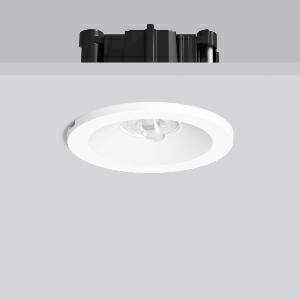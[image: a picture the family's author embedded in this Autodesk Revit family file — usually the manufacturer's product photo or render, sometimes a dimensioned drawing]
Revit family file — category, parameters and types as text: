
# Revit family: turia_l_672561_002_07_3232
name_source: partatom
category: Lighting Fixtures
units: mm (PartAtom-declared; Revit-internal decimal feet)

## family parameters
Cut with Voids When Loaded = No
Host = Face
Light Source = No
Part Type = Normal
Room Calculation Point = No
Round Connector Dimension = Use Diameter
Shared = No

## types (1)
- TURIA L (1 x LED Modul 765, 270 lm, 6500)
    Apparent Load = 5 VA
    CIE Flux Codes = 70 91 99 100 100
    Color Rendering = 70
    Color Temperature = 6500
    Default Elevation = 1800 mm
    Description = Series: TURIA L
Round emergency luminaire for escape route lighting. Housing: die-cast aluminium. Bezel ring: plastic. With asymmetrical beam plastic lenses for illuminating rescue facilities. Self-contained system with automatic self-test and feedback via DALI bus, only to RZB DALI monitoring system. With enclosed separate ceiling mounting ring also suitable for ceiling cut-outs of Ø 68 mm. 
Colour: white
Diameter: 62 mm
Height: 3 mm
Cut-out diameter: 54-68 mm
Recess height: 76-162 mm
Luminaire: recess height: 42 mm
Weight: 430 g
Operating mode: non-maintained power mode
Duration time: 3 h
Lamp: LED
Socket: without socket
Colour temperature: 6500K
Colour rendering index (CRI): 70
System power: 5.2 W
Rated luminous flux: 270 lm
Luminous flux, emergency: 190 lm
System power, emergency: -
Control gear: Regulated power supply
Protection class: II
Type of protection: IP 20
    Height = 0 mm  [stored 0 ft]
    Lamp = 1 x LED Modul 765
    Lamp Light Flux = 270 lm
    Lamp count = 1
    Length = 62 mm  [stored 0.203412 ft]
    Lifetime = 50000 h
    Luminous efficacy = 52 lm/W
    Manufacturer = RZB
    ModVariant = No
    Model = 672561.002.07
    Mounting Place = Ceiling
    Mounting Type = Recessed
    Number of Poles = 1
    OnlyDefault = Yes
    Power Factor = 1
    Product Name = TURIA L
    Product group = Recessed ceiling luminaires
    ProductGroupID = 405
    Protection Class = Protection class II
    Protection Degree = IP 20
    RLX_Detail_Level = 1
    RLX_Emergency_Light_Flux = 190 lm
    RLX_Emergency_Type = 3
    RLX_Emergency_Type_DB = Yes
    RlxData = <blob elided: 55229 chars, md5=2dcdf614>
    Socket = socket
    Standby Power = 0 W
    System Light Flux = 270 lm
    System Power = 5 W
    Type Comments = Product without accessories
    Type Image = 672561.002.jpg
    URL = http://relux.com
    VarID = ---
    Voltage = 230 V
    Voltage Range = 220-240 V
    Weight = 0.00 kg
    Width = 0 mm  [stored 0 ft]

note: [stored X ft] marks values corroborated as IEEE doubles in the binary element streams (Revit-internal decimal feet)

## geometry (parser evidence)
native form markers: Blend x4, Sweep x12
no freeform markers — native parametric forms only
